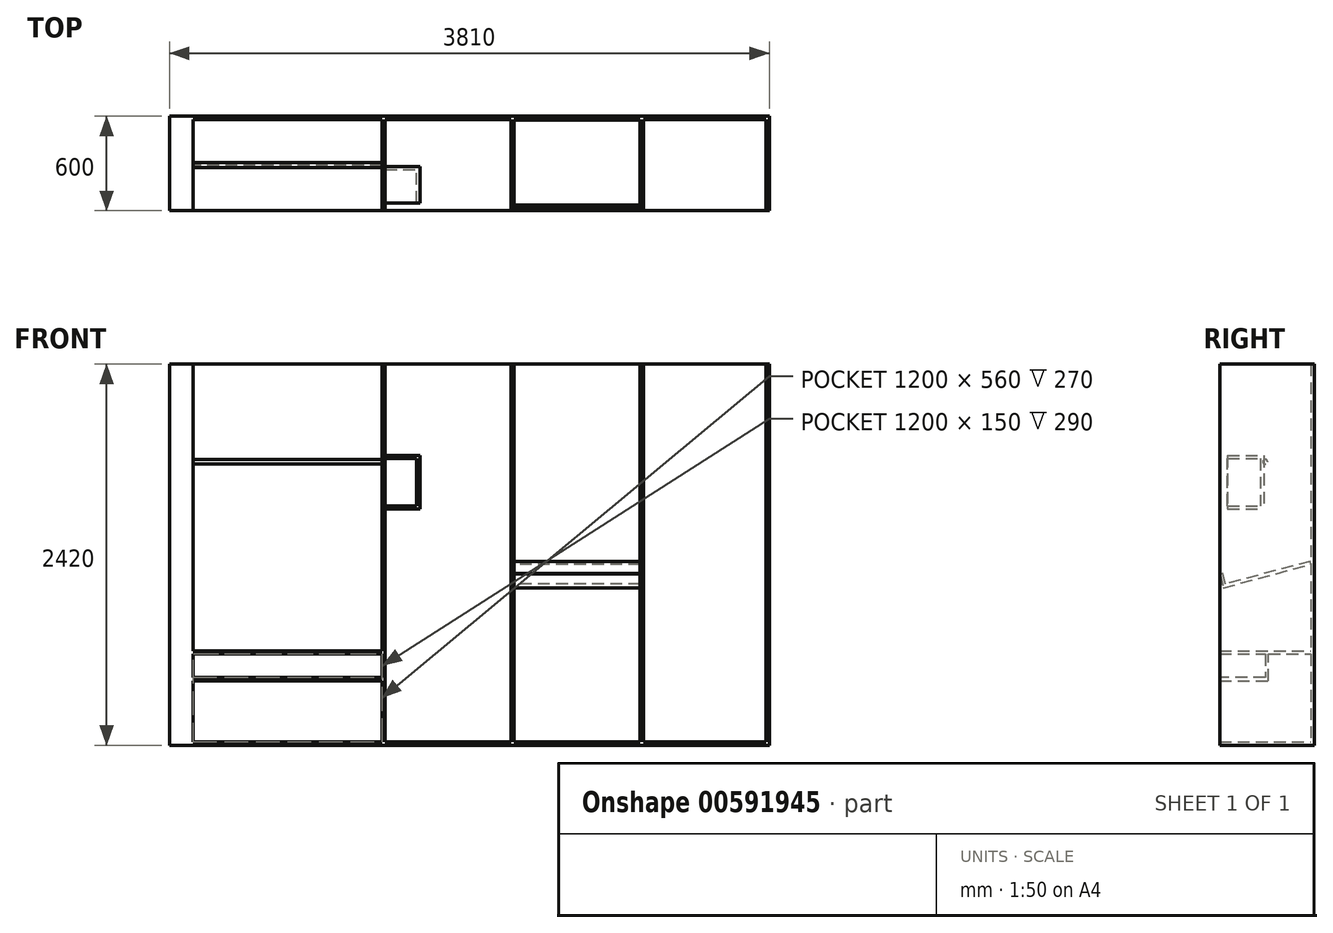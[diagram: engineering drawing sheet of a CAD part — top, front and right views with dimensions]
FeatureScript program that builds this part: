
annotation { "Feature Type Name" : "Feature", "Feature Type Description" : "" }
export const myFeature = defineFeature(function(context is Context, id is Id, definition is map)
    precondition{}
    {
        {
            var Q0;
            Q0=qCreatedBy(makeId("Front.planeOp"),FACE);
            var sketch = newSketch(context, id + "F0", { "sketchPlane" : qUnion([Q0])});
            skLineSegment(sketch, "E0.top", {"start": v(1420, -1200) * mm, "end": v(620, -1200) * mm});
            skLineSegment(sketch, "E0.left", {"start": v(1420, 1200) * mm, "end": v(1420, -1200) * mm});
            skLineSegment(sketch, "E0.right", {"start": v(-1420, 1200) * mm, "end": v(-1420, -1200) * mm});
            skPoint(sketch, "E0.middle", {"position": v(0, 0) * mm});
            skLineSegment(sketch, "E1", {"start": v(-220, 1200) * mm, "end": v(-220, -1200) * mm});
            skLineSegment(sketch, "E2", {"start": v(600, 1200) * mm, "end": v(600, -1200) * mm});
            skLineSegment(sketch, "E3.0", {"start": v(-1440, 1200) * mm, "end": v(-1440, -1220) * mm});
            skLineSegment(sketch, "E3.2", {"start": v(1440, 1200) * mm, "end": v(1440, -1220) * mm});
            skLineSegment(sketch, "E3.3", {"start": v(1440, -1220) * mm, "end": v(-1440, -1220) * mm});
            skLineSegment(sketch, "E4.0", {"start": v(620, 1200) * mm, "end": v(620, -1200) * mm});
            skLineSegment(sketch, "E5.0", {"start": v(-200, 1200) * mm, "end": v(-200, -1200) * mm});
            skLineSegment(sketch, "E6.trimOffspring", {"start": v(600, -1200) * mm, "end": v(-200, -1200) * mm});
            skLineSegment(sketch, "E7.trimOffspring", {"start": v(-220, -1200) * mm, "end": v(-1420, -1200) * mm});
            skLineSegment(sketch, "E8", {"start": v(-1440, 1200) * mm, "end": v(-1570, 1200) * mm});
            skLineSegment(sketch, "E9", {"start": v(-1570, 1200) * mm, "end": v(-1570, -1220) * mm});
            skLineSegment(sketch, "E10", {"start": v(-1570, -1220) * mm, "end": v(-1440, -1220) * mm});
            skLineSegment(sketch, "E11", {"start": v(1420, 1200) * mm, "end": v(1440, 1200) * mm});
            skLineSegment(sketch, "E12", {"start": v(600, 1200) * mm, "end": v(620, 1200) * mm});
            skLineSegment(sketch, "E13", {"start": v(-200, 1200) * mm, "end": v(-220, 1200) * mm});
            skLineSegment(sketch, "E14", {"start": v(-1440, 1200) * mm, "end": v(-1420, 1200) * mm});
            skLineSegment(sketch, "E15", {"start": v(-1420, 1200) * mm, "end": v(-220, 1200) * mm});
            skLineSegment(sketch, "E16", {"start": v(1420, 1200) * mm, "end": v(620, 1200) * mm});
            skLineSegment(sketch, "E17", {"start": v(-200, 1200) * mm, "end": v(600, 1200) * mm});
            skSolve(sketch);
        }
        {
            var Q0;
            Q0=makeQuery(id+"F0.imprint","IMPRINT",FACE,{"disambiguationData":[TD([[makeQuery(id+"F0.imprint","IMPRINT",EDGE,{"derivedFrom":sQuery(id+"F0.wireOp",EDGE,"E0.right")}),1.0]])]});
            var Q1;
            Q1=makeQuery(id+"F0.imprint","IMPRINT",FACE,{"disambiguationData":[TD([[makeQuery(id+"F0.imprint","IMPRINT",EDGE,{"derivedFrom":sQuery(id+"F0.wireOp",EDGE,"E3.0")}),-1.0]])]});
            var Q2;
            Q2=makeQuery(id+"F0.imprint","IMPRINT",FACE,{"disambiguationData":[TD([[makeQuery(id+"F0.imprint","IMPRINT",EDGE,{"derivedFrom":sQuery(id+"F0.wireOp",EDGE,"E2")}),-1.0]])]});
            var Q3;
            Q3=makeQuery(id+"F0.imprint","IMPRINT",FACE,{"disambiguationData":[TD([[makeQuery(id+"F0.imprint","IMPRINT",EDGE,{"derivedFrom":sQuery(id+"F0.wireOp",EDGE,"E0.top")}),-1.0]])]});
            var Q4;
            Q4=makeQuery(id+"F0.imprint","IMPRINT",FACE,{"disambiguationData":[TD([[makeQuery(id+"F0.imprint","IMPRINT",EDGE,{"derivedFrom":sQuery(id+"F0.wireOp",EDGE,"E0.top")}),1.0]])]});
            extrude(context, id + "F1", {"entities" : qUnion([Q0, Q1, Q2, Q3, Q4]), "depth" : 600 * mm, "offsetDistance" : 25 * mm});
        }
        {
            var Q0;
            Q0=makeQuery(id+"F0.imprint","IMPRINT",FACE,{"disambiguationData":[TD([[makeQuery(id+"F0.imprint","IMPRINT",EDGE,{"derivedFrom":sQuery(id+"F0.wireOp",EDGE,"E0.top")}),-1.0]])]});
            var Q1;
            Q1=makeQuery(id+"F0.imprint","IMPRINT",FACE,{"disambiguationData":[TD([[makeQuery(id+"F0.imprint","IMPRINT",EDGE,{"derivedFrom":sQuery(id+"F0.wireOp",EDGE,"E2")}),-1.0]])]});
            var Q2;
            Q2=makeQuery(id+"F0.imprint","IMPRINT",FACE,{"disambiguationData":[TD([[makeQuery(id+"F0.imprint","IMPRINT",EDGE,{"derivedFrom":sQuery(id+"F0.wireOp",EDGE,"E0.right")}),1.0]])]});
            extrude(context, id + "F2", {"entities" : qUnion([Q0, Q1, Q2]), "operationType" : NewBodyOperationType.REMOVE, "depth" : 600 * mm, "offsetDistance" : 25 * mm, "hasSecondDirection" : true, "secondDirectionOppositeDirection" : false, "secondDirectionDepth" : 20 * mm});
        }
        {
            var Q0;
            Q0=makeQuery(id+"F2.boolean.opBoolean","COPY",FACE,{"derivedFrom":makeQuery(id+"F2.opExtrude","SWEPT_FACE",FACE,{"disambiguationData":[OSD([sQuery(id+"F0.wireOp",EDGE,"E0.right")])]})});
            var sketch = newSketch(context, id + "F3", { "sketchPlane" : qUnion([Q0])});
            skLineSegment(sketch, "E18", {"start": v(-600, 580) * mm, "end": v(-20, 580) * mm, "construction": true});
            skCircle(sketch, "E19", {"center": v(-310, 580) * mm, "radius": 15 * mm});
            skLineSegment(sketch, "E20.bottom", {"start": v(-600, 950) * mm, "end": v(-20, 950) * mm});
            skLineSegment(sketch, "E20.top", {"start": v(-600, 930) * mm, "end": v(-20, 930) * mm});
            skLineSegment(sketch, "E20.left", {"start": v(-600, 950) * mm, "end": v(-600, 930) * mm});
            skLineSegment(sketch, "E20.right", {"start": v(-20, 950) * mm, "end": v(-20, 930) * mm});
            skLineSegment(sketch, "E21.bottom", {"start": v(-600, -620) * mm, "end": v(-20, -620) * mm});
            skLineSegment(sketch, "E21.top", {"start": v(-600, -640) * mm, "end": v(-310, -640) * mm});
            skLineSegment(sketch, "E21.left", {"start": v(-600, -620) * mm, "end": v(-600, -640) * mm});
            skLineSegment(sketch, "E21.right", {"start": v(-20, -620) * mm, "end": v(-20, -640) * mm});
            skLineSegment(sketch, "E22", {"start": v(-310, -640) * mm, "end": v(-310, -790) * mm});
            skLineSegment(sketch, "E23", {"start": v(-310, -790) * mm, "end": v(-600, -790) * mm});
            skLineSegment(sketch, "E24", {"start": v(-600, -790) * mm, "end": v(-600, -810) * mm});
            skLineSegment(sketch, "E25", {"start": v(-600, -810) * mm, "end": v(-290, -810) * mm});
            skLineSegment(sketch, "E26", {"start": v(-290, -810) * mm, "end": v(-290, -640) * mm});
            skLineSegment(sketch, "E27.trimOffspring", {"start": v(-290, -640) * mm, "end": v(-20, -640) * mm});
            skSolve(sketch);
        }
        {
            var Q0;
            Q0=makeQuery(id+"F3.imprint","IMPRINT",FACE,{"disambiguationData":[TD([[makeQuery(id+"F3.imprint","IMPRINT",EDGE,{"derivedFrom":sQuery(id+"F3.wireOp",EDGE,"E19")}),1.0]])]});
            var Q1;
            Q1=makeQuery(id+"F3.imprint","IMPRINT",FACE,{"disambiguationData":[TD([[makeQuery(id+"F3.imprint","IMPRINT",EDGE,{"derivedFrom":sQuery(id+"F3.wireOp",EDGE,"E21.bottom")}),-1.0]])]});
            extrude(context, id + "F4", {"entities" : qUnion([Q0, Q1]), "operationType" : NewBodyOperationType.ADD, "endBound" : BoundingType.UP_TO_NEXT, "depth" : 25 * mm, "offsetDistance" : 25 * mm});
        }
        {
            var Q0;
            Q0=makeQuery(id+"F2.boolean.opBoolean","COPY",FACE,{"derivedFrom":makeQuery(id+"F2.opExtrude","SWEPT_FACE",FACE,{"disambiguationData":[OSD([sQuery(id+"F0.wireOp",EDGE,"E5.0")])]})});
            var sketch = newSketch(context, id + "F5", { "sketchPlane" : qUnion([Q0])});
            skLineSegment(sketch, "E28", {"start": v(-600, -133.07) * mm, "end": v(-576.7, -220) * mm});
            skLineSegment(sketch, "E29", {"start": v(-576.7, -220) * mm, "end": v(-20, -70.83) * mm});
            skLineSegment(sketch, "E30", {"start": v(-20, -70.83) * mm, "end": v(-25.18, -51.51) * mm});
            skLineSegment(sketch, "E31", {"start": v(-25.18, -51.51) * mm, "end": v(-562.56, -195.5) * mm});
            skLineSegment(sketch, "E32", {"start": v(-562.56, -195.5) * mm, "end": v(-580.68, -127.9) * mm});
            skLineSegment(sketch, "E33", {"start": v(-580.68, -127.9) * mm, "end": v(-600, -133.07) * mm});
            skSolve(sketch);
        }
        {
            var Q0;
            Q0=makeQuery(id+"F5.imprint","IMPRINT",FACE,{"disambiguationData":[TD([[makeQuery(id+"F5.imprint","IMPRINT",EDGE,{"derivedFrom":sQuery(id+"F5.wireOp",EDGE,"E28")}),1.0]])]});
            var Q1;
            Q1=makeQuery(id+"F2.boolean.opBoolean","COPY",FACE,{"derivedFrom":makeQuery(id+"F2.opExtrude","SWEPT_FACE",FACE,{"disambiguationData":[OSD([sQuery(id+"F0.wireOp",EDGE,"E0.left")])]})});
            var Q2;
            Q2=makeQuery(id+"F2.boolean.opBoolean","COPY",FACE,{"derivedFrom":makeQuery(id+"F2.opExtrude","SWEPT_FACE",FACE,{"disambiguationData":[OSD([sQuery(id+"F0.wireOp",EDGE,"E4.0")])]})});
            extrude(context, id + "F6", {"entities" : qUnion([Q0]), "endBound" : BoundingType.UP_TO_SURFACE, "depth" : 25 * mm, "endBoundEntityFace" : qUnion([Q1]), "offsetDistance" : 25 * mm, "hasSecondDirection" : true, "secondDirectionBound" : SecondDirectionBoundingType.UP_TO_SURFACE, "secondDirectionOppositeDirection" : false, "secondDirectionDepth" : 25 * mm, "secondDirectionBoundEntityFace" : qUnion([Q2])});
        }
        {
            var Q0;
            Q0=makeQuery(id+"F2.boolean.opBoolean","COPY",FACE,{"derivedFrom":makeQuery(id+"F2.opExtrude","CAP_FACE",FACE,{"disambiguationData":[OSD([sQuery(id+"F0.wireOp",EDGE,"E2"),sQuery(id+"F0.wireOp",EDGE,"E5.0"),sQuery(id+"F0.wireOp",EDGE,"E6.trimOffspring"),sQuery(id+"F0.wireOp",EDGE,"E17")])],"isStart":true})});
            var sketch = newSketch(context, id + "F7", { "sketchPlane" : qUnion([Q0])});
            skLineSegment(sketch, "E34.bottom", {"start": v(3361.99, 247.25) * mm, "end": v(3256.6, 247.25) * mm});
            skLineSegment(sketch, "E34.top", {"start": v(3361.99, 163.88) * mm, "end": v(3256.6, 163.88) * mm});
            skLineSegment(sketch, "E34.left", {"start": v(3361.99, 247.25) * mm, "end": v(3361.99, 163.88) * mm});
            skLineSegment(sketch, "E34.right", {"start": v(3256.6, 247.25) * mm, "end": v(3256.6, 163.88) * mm});
            skLineSegment(sketch, "E35.bottom", {"start": v(-200, 600) * mm, "end": v(0, 600) * mm});
            skLineSegment(sketch, "E35.top", {"start": v(-200, 300) * mm, "end": v(0, 300) * mm});
            skLineSegment(sketch, "E35.left", {"start": v(-200, 600) * mm, "end": v(-200, 300) * mm});
            skLineSegment(sketch, "E35.right", {"start": v(0, 600) * mm, "end": v(0, 300) * mm});
            skLineSegment(sketch, "E36.0", {"start": v(-200, 280) * mm, "end": v(20, 280) * mm});
            skLineSegment(sketch, "E36.1", {"start": v(20, 620) * mm, "end": v(20, 280) * mm});
            skLineSegment(sketch, "E36.2", {"start": v(-200, 620) * mm, "end": v(20, 620) * mm});
            skSolve(sketch);
        }
        {
            var Q0;
            {var subQ3=sQuery(id+"F7.wireOp",EDGE,"E35.bottom");Q0=makeQuery(id+"F7.imprint","IMPRINT",FACE,{"disambiguationData":[TD([[makeQuery(id+"F7.imprint","IMPRINT",EDGE,{"derivedFrom":subQ3}),1.0]])]});}
            var Q1;
            Q1=makeQuery(id+"F7.imprint","IMPRINT",FACE,{"disambiguationData":[TD([[makeQuery(id+"F7.imprint","IMPRINT",EDGE,{"derivedFrom":sQuery(id+"F7.wireOp",EDGE,"E35.bottom")}),-1.0]])]});
            var Q2;
            Q2=makeQuery(id+"F4.boolean.opBoolean","MERGE",FACE,{"derivedFrom":[makeQuery(id+"F1.opExtrude","CAP_FACE",FACE,{"disambiguationData":[OSD([sQuery(id+"F0.wireOp",EDGE,"E3.2"),sQuery(id+"F0.wireOp",EDGE,"E3.3"),sQuery(id+"F0.wireOp",EDGE,"E8"),sQuery(id+"F0.wireOp",EDGE,"E9"),sQuery(id+"F0.wireOp",EDGE,"E10"),sQuery(id+"F0.wireOp",EDGE,"E11"),sQuery(id+"F0.wireOp",EDGE,"E12"),sQuery(id+"F0.wireOp",EDGE,"E13"),sQuery(id+"F0.wireOp",EDGE,"E14"),sQuery(id+"F0.wireOp",EDGE,"E15"),sQuery(id+"F0.wireOp",EDGE,"E16"),sQuery(id+"F0.wireOp",EDGE,"E17")])],"isStart":false}),makeQuery(id+"F4.opExtrude","SWEPT_FACE",FACE,{"disambiguationData":[OSD([sQuery(id+"F3.wireOp",EDGE,"E21.left")])]}),makeQuery(id+"F4.opExtrude","SWEPT_FACE",FACE,{"disambiguationData":[OSD([sQuery(id+"F3.wireOp",EDGE,"E24")])]})]});
            extrude(context, id + "F8", {"entities" : qUnion([Q0, Q1]), "operationType" : NewBodyOperationType.ADD, "endBound" : BoundingType.UP_TO_SURFACE, "depth" : 400 * mm, "endBoundEntityFace" : qUnion([Q2]), "hasOffset" : true, "offsetDistance" : 50 * mm, "hasSecondDirection" : true, "secondDirectionOppositeDirection" : false, "secondDirectionDepth" : 300 * mm});
        }
        {
            var Q0;
            Q0=makeQuery(id+"F7.imprint","IMPRINT",FACE,{"disambiguationData":[TD([[makeQuery(id+"F7.imprint","IMPRINT",EDGE,{"derivedFrom":sQuery(id+"F7.wireOp",EDGE,"E35.bottom")}),-1.0]])]});
            var Q1;
            {var subQ0=sQuery(id+"F3.wireOp",EDGE,"E24");var subQ1=sQuery(id+"F3.wireOp",EDGE,"E21.left");var subQ2=sQuery(id+"F0.wireOp",EDGE,"E17");var subQ3=sQuery(id+"F0.wireOp",EDGE,"E16");var subQ4=sQuery(id+"F0.wireOp",EDGE,"E15");var subQ5=sQuery(id+"F0.wireOp",EDGE,"E14");var subQ6=sQuery(id+"F0.wireOp",EDGE,"E13");var subQ7=sQuery(id+"F0.wireOp",EDGE,"E12");var subQ8=sQuery(id+"F0.wireOp",EDGE,"E11");var subQ9=sQuery(id+"F0.wireOp",EDGE,"E10");var subQ10=sQuery(id+"F0.wireOp",EDGE,"E9");var subQ11=sQuery(id+"F0.wireOp",EDGE,"E8");var subQ12=sQuery(id+"F0.wireOp",EDGE,"E3.3");var subQ13=sQuery(id+"F0.wireOp",EDGE,"E3.2");Q1=makeQuery(id+"F8.boolean.opBoolean","MERGE",FACE,{"derivedFrom":[makeQuery(id+"F4.boolean.opBoolean","MERGE",FACE,{"derivedFrom":[makeQuery(id+"F1.opExtrude","CAP_FACE",FACE,{"disambiguationData":[OSD([subQ13,subQ12,subQ11,subQ10,subQ9,subQ8,subQ7,subQ6,subQ5,subQ4,subQ3,subQ2])],"isStart":false}),makeQuery(id+"F4.opExtrude","SWEPT_FACE",FACE,{"disambiguationData":[OSD([subQ1])]}),makeQuery(id+"F4.opExtrude","SWEPT_FACE",FACE,{"disambiguationData":[OSD([subQ0])]})]}),makeQuery(id+"F8.opExtrude","CAP_FACE",FACE,{"disambiguationData":[OSD([subQ13,subQ12,subQ11,subQ10,subQ9,subQ8,subQ7,subQ6,subQ5,subQ4,subQ3,subQ2,subQ1,subQ0])],"isStart":false})]});}
            var Q2;
            Q2=makeQuery(id+"F8.opExtrude","CAP_FACE",FACE,{"disambiguationData":[OSD([sQuery(id+"F0.wireOp",EDGE,"E5.0"),sQuery(id+"F7.wireOp",EDGE,"E35.left"),sQuery(id+"F7.wireOp",EDGE,"E36.0"),sQuery(id+"F7.wireOp",EDGE,"E36.1"),sQuery(id+"F7.wireOp",EDGE,"E36.2")])],"isStart":true});
            extrude(context, id + "F9", {"entities" : qUnion([Q0]), "operationType" : NewBodyOperationType.REMOVE, "endBound" : BoundingType.UP_TO_SURFACE, "depth" : 25 * mm, "endBoundEntityFace" : qUnion([Q1]), "offsetDistance" : 25 * mm, "hasSecondDirection" : true, "secondDirectionBound" : SecondDirectionBoundingType.UP_TO_SURFACE, "secondDirectionOppositeDirection" : false, "secondDirectionDepth" : 25 * mm, "secondDirectionBoundEntityFace" : qUnion([Q2]), "hasSecondDirectionOffset" : true, "secondDirectionOffsetDistance" : 20 * mm, "secondDirectionOffsetOppositeDirection" : true});
        }
        {
            var Q0;
            Q0=qCreatedBy(makeId("Front.planeOp"),FACE);
            var sketch = newSketch(context, id + "F10", { "sketchPlane" : qUnion([Q0])});
            skLineSegment(sketch, "E37.bottom", {"start": v(1440, -1220) * mm, "end": v(2240, -1220) * mm});
            skLineSegment(sketch, "E37.top", {"start": v(1440, 1200) * mm, "end": v(2240, 1200) * mm});
            skLineSegment(sketch, "E37.left", {"start": v(1440, -1220) * mm, "end": v(1440, 1200) * mm});
            skLineSegment(sketch, "E37.right", {"start": v(2240, -1220) * mm, "end": v(2240, 1200) * mm});
            skLineSegment(sketch, "E38.0", {"start": v(2220, -1200) * mm, "end": v(2220, 1200) * mm});
            skLineSegment(sketch, "E38.1", {"start": v(1440, -1200) * mm, "end": v(2220, -1200) * mm});
            skSolve(sketch);
        }
        {
            var Q0;
            Q0 = qSketchRegion(id + "F10", true);
            extrude(context, id + "F11", {"entities" : qUnion([Q0]), "operationType" : NewBodyOperationType.ADD, "depth" : 600 * mm, "offsetDistance" : 25 * mm});
        }
        {
            var Q0;
            {var subQ3=sQuery(id+"F10.wireOp",EDGE,"E38.0");Q0=makeQuery(id+"F10.imprint","IMPRINT",FACE,{"disambiguationData":[TD([[makeQuery(id+"F10.imprint","IMPRINT",EDGE,{"derivedFrom":subQ3}),1.0]])]});}
            extrude(context, id + "F12", {"entities" : qUnion([Q0]), "operationType" : NewBodyOperationType.REMOVE, "endBound" : BoundingType.UP_TO_NEXT, "depth" : 25 * mm, "offsetDistance" : 25 * mm, "offsetOppositeDirection" : true, "hasSecondDirection" : true, "secondDirectionOppositeDirection" : false, "secondDirectionDepth" : 20 * mm});
        }
    });
